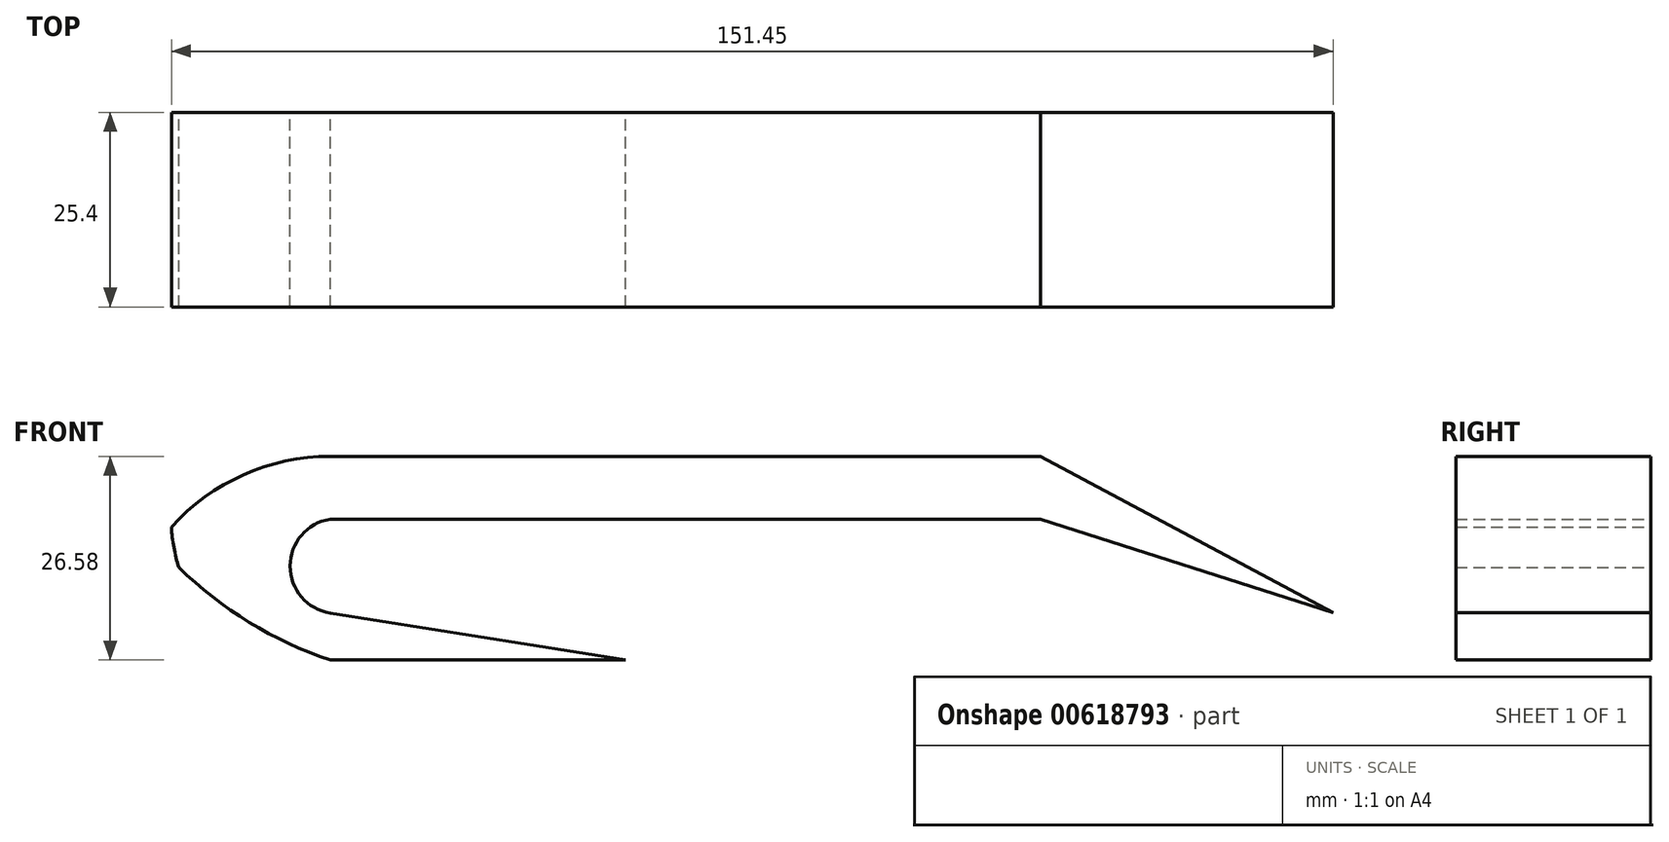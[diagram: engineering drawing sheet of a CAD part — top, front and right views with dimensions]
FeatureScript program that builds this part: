
annotation { "Feature Type Name" : "Feature", "Feature Type Description" : "" }
export const myFeature = defineFeature(function(context is Context, id is Id, definition is map)
    precondition{}
    {
        {
            var Q0;
            Q0=qCreatedBy(makeId("Front.planeOp"),FACE);
            var sketch = newSketch(context, id + "F0", { "sketchPlane" : qUnion([Q0])});
            skLineSegment(sketch, "E0", {"start": v(54.13, 0) * mm, "end": v(-38.5, 0) * mm});
            skLineSegment(sketch, "E1", {"start": v(54.13, 8.19) * mm, "end": v(-38.5, 8.19) * mm});
            skArc(sketch, "E2", {"start": v(-59.2, -1.04) * mm, "mid": v(-58.88, -3.7) * mm, "end": v(-58.23, -6.3) * mm});
            skArc(sketch, "E3", {"start": v(-38.5, 8.19) * mm, "mid": v(-49.83, 5.78) * mm, "end": v(-59.2, -1.04) * mm});
            skArc(sketch, "E4", {"start": v(-58.23, -6.3) * mm, "mid": v(-49.05, -13.46) * mm, "end": v(-38.5, -18.4) * mm});
            skLineSegment(sketch, "E5", {"start": v(-38.5, -18.4) * mm, "end": v(0, -18.4) * mm});
            skLineSegment(sketch, "E6", {"start": v(0, -18.4) * mm, "end": v(-38.5, -12.26) * mm});
            skArc(sketch, "E7", {"start": v(-38.5, 0) * mm, "mid": v(-43.73, -6.13) * mm, "end": v(-38.5, -12.26) * mm});
            skLineSegment(sketch, "E8", {"start": v(54.13, 0) * mm, "end": v(92.26, -12.22) * mm});
            skLineSegment(sketch, "E9", {"start": v(92.26, -12.22) * mm, "end": v(54.13, 8.19) * mm});
            skSolve(sketch);
        }
        {
            var Q0;
            Q0 = qSketchRegion(id + "F0", true);
            extrude(context, id + "F1", {"entities" : qUnion([Q0]), "depth" : 25.4 * mm, "offsetDistance" : 25.4 * mm});
        }
        {
            var Q0;
            Q0=sQuery(id+"F0.wireOp",EDGE,"E1");
            var Q1;
            Q1=sQuery(id+"F0.wireOp",EDGE,"E6");
            var Q2;
            Q2=sQuery(id+"F0.wireOp",EDGE,"E3");
            var Q3;
            Q3=sQuery(id+"F0.wireOp",EDGE,"E8");
            var Q4;
            Q4=sQuery(id+"F0.wireOp",EDGE,"E9");
            var Q5;
            Q5=sQuery(id+"F0.wireOp",EDGE,"E4");
            var Q6;
            Q6=sQuery(id+"F0.wireOp",EDGE,"E0");
            var Q7;
            Q7=sQuery(id+"F0.wireOp",EDGE,"E5");
            var Q8;
            Q8=sQuery(id+"F0.wireOp",EDGE,"E7");
            var Q9;
            Q9=sQuery(id+"F0.wireOp",EDGE,"E2");
            extrude(context, id + "F2", {"bodyType" : ToolBodyType.SURFACE, "surfaceEntities" : qUnion([Q0, Q1, Q2, Q3, Q4, Q5, Q6, Q7, Q8, Q9]), "depth" : 25.4 * mm, "offsetDistance" : 25.4 * mm});
        }
    });
